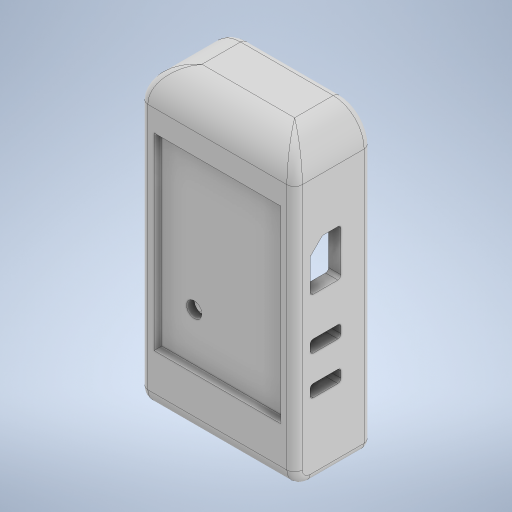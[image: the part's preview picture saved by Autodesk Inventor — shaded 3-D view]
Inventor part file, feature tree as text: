
AUTODESK INVENTOR PART (.ipt)
format: ipt  version: 2024 (Build 280153000, 153)  size: 533,504 bytes
history: native  units: mm
features: sketch x12, extrude x11, fillet x4, other x1
ambient origin geometry x8: Origin, YZ Plane, XZ Plane, XY Plane, X Axis, Y Axis, Z Axis, Center Point
bodies: Body1 (feature_tree)
feature tree (28):
  other  "Těleso1"
  extrude  "Vysunutí1"  Depth=100.0mm
  sketch  "Náčrt2"
  extrude  "Vysunutí3"  Depth=190.0mm
  fillet  "Zaoblení1"  Radius=50.0mm
  fillet  "Zaoblení2"  Radius=84.0mm
  extrude  "Vysunutí4"  Depth=110.0mm
  extrude  "Vysunutí5"  Depth=40.0mm TaperAngle=0.0deg
  extrude  "Vysunutí6"  Depth=20.0mm
  extrude  "Vysunutí8"  Depth=10.0mm
  fillet  "Zaoblení3"  Radius=20.0mm
  fillet  "Zaoblení4"  Radius=40.0mm
  extrude  "Vysunutí12"  Depth=5.0mm
  extrude  "Vysunutí13"  Depth=5.0mm
  extrude  "Vysunutí15"  Depth=5.0mm
  extrude  "Vysunutí16"  Depth=5.0mm
  extrude  "Vysunutí17"  Depth=10.0mm TaperAngle=0.0deg
  sketch  "Náčrt1"
  sketch  "Náčrt4"
  sketch  "Náčrt5"
  sketch  "Náčrt6"
  sketch  "Náčrt9"
  sketch  "Náčrt11"
  sketch  "Náčrt17"
  sketch  "Náčrt18"
  sketch  "Náčrt20"
  sketch  "Náčrt21"
  sketch  "Náčrt25"
